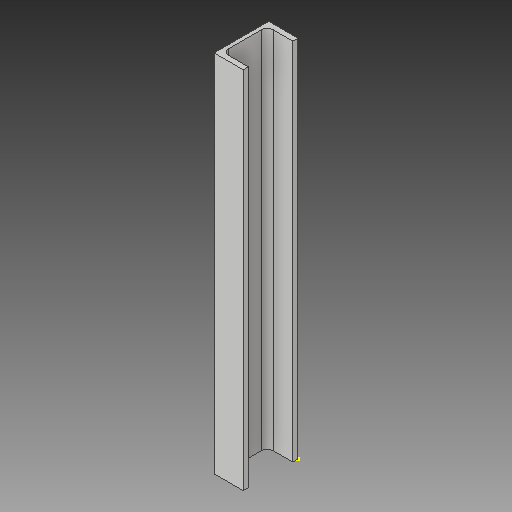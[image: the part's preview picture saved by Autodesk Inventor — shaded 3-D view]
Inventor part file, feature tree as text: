
AUTODESK INVENTOR PART (.ipt)
format: ipt  version: 2019 (Build 230136000, 136)  size: 93,184 bytes
history: native  units: in
note: dims shown in document units (in); Inventor stores cm internally (conversion verified against a paired STEP export)
features: other x3, sketch x2
ambient origin geometry x8: Origin, YZ Plane, XZ Plane, XY Plane, X Axis, Y Axis, Z Axis, Center Point
bodies: Solid1 (feature_tree)
feature tree (5):
  other  "Channel2_MIR_MIR.ipt"
  other  "Solid1::Channel2_MIR_MIR.ipt"
  other  "TaggingFeature1"
  sketch  "Sketch1"  dims[d0=0.3937in]
  sketch  "Sketch2"
